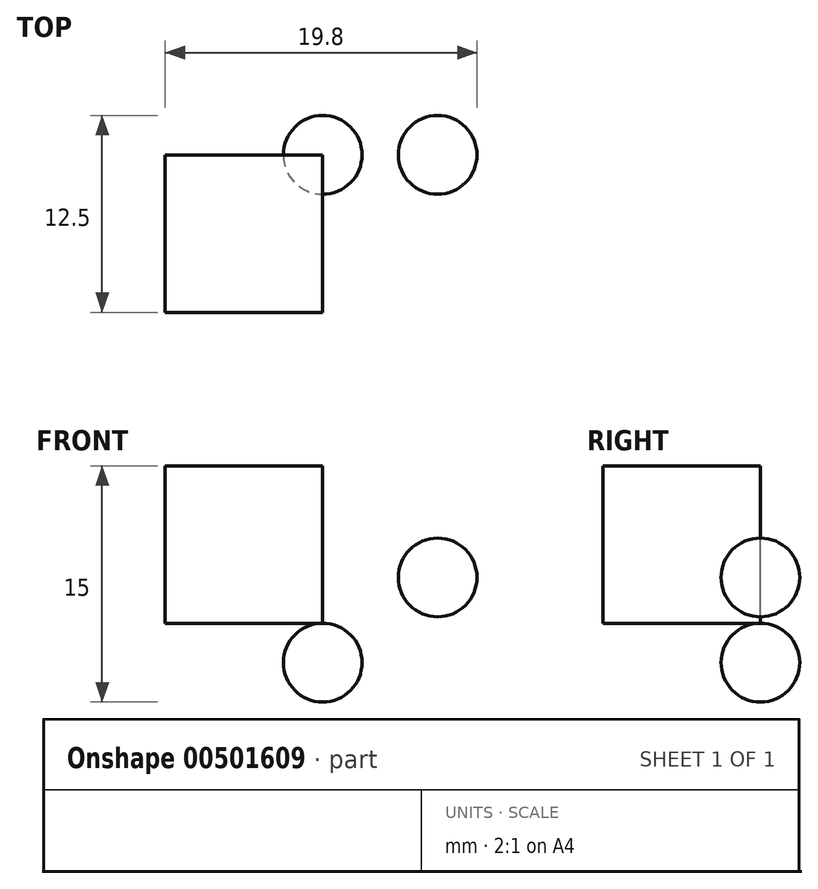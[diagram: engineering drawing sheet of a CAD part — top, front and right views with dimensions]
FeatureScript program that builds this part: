
annotation { "Feature Type Name" : "Feature", "Feature Type Description" : "" }
export const myFeature = defineFeature(function(context is Context, id is Id, definition is map)
    precondition{}
    {
        {
            var Q0;
            Q0=qCreatedBy(makeId("Front.planeOp"),FACE);
            var sketch = newSketch(context, id + "F0", { "sketchPlane" : qUnion([Q0])});
            skLineSegment(sketch, "E0.bottom", {"start": v(0, 0) * mm, "end": v(-10, 0) * mm});
            skLineSegment(sketch, "E0.top", {"start": v(0, 10) * mm, "end": v(-10, 10) * mm});
            skLineSegment(sketch, "E0.left", {"start": v(0, 0) * mm, "end": v(0, 10) * mm});
            skLineSegment(sketch, "E0.right", {"start": v(-10, 0) * mm, "end": v(-10, 10) * mm});
            skSolve(sketch);
        }
        {
            var Q0;
            Q0 = qSketchRegion(id + "F0", true);
            extrude(context, id + "F1", {"entities" : qUnion([Q0]), "depth" : 10 * mm});
        }
        {
            var Q0;
            Q0=qCreatedBy(makeId("Front.planeOp"),FACE);
            var sketch = newSketch(context, id + "F2", { "sketchPlane" : qUnion([Q0])});
            skLineSegment(sketch, "E1", {"start": v(0, 0) * mm, "end": v(0, -5) * mm});
            skArc(sketch, "E2", {"start": v(0, 0) * mm, "mid": v(-2.5, -2.5) * mm, "end": v(0, -5) * mm});
            skSolve(sketch);
        }
        {
            var Q0;
            Q0=makeQuery(id+"F2.imprint","IMPRINT",FACE,{"disambiguationData":[TD([[makeQuery(id+"F2.imprint","IMPRINT",EDGE,{"derivedFrom":sQuery(id+"F2.wireOp",EDGE,"E1")}),-1.0]])]});
            var Q1;
            Q1=sQuery(id+"F2.wireOp",EDGE,"E1");
            revolve(context, id + "F3", {"entities" : qUnion([Q0]), "axis" : qUnion([Q1]), "revolveType" : RevolveType.FULL});
        }
        {
            var Q0;
            Q0=makeQuery(id+"F3.opRevolve","SWEPT_BODY",BODY,{"disambiguationData":[OSD([sQuery(id+"F2.wireOp",EDGE,"E1"),sQuery(id+"F2.wireOp",EDGE,"E2")])]});
            transform(context, id + "F4", {"entities" : qUnion([Q0]), "transformType" : TransformType.TRANSLATION_3D, "dx" : 7.3 * mm, "dy" : 0 * mm, "dz" : 5.4 * mm, "makeCopy" : true});
        }
    });
